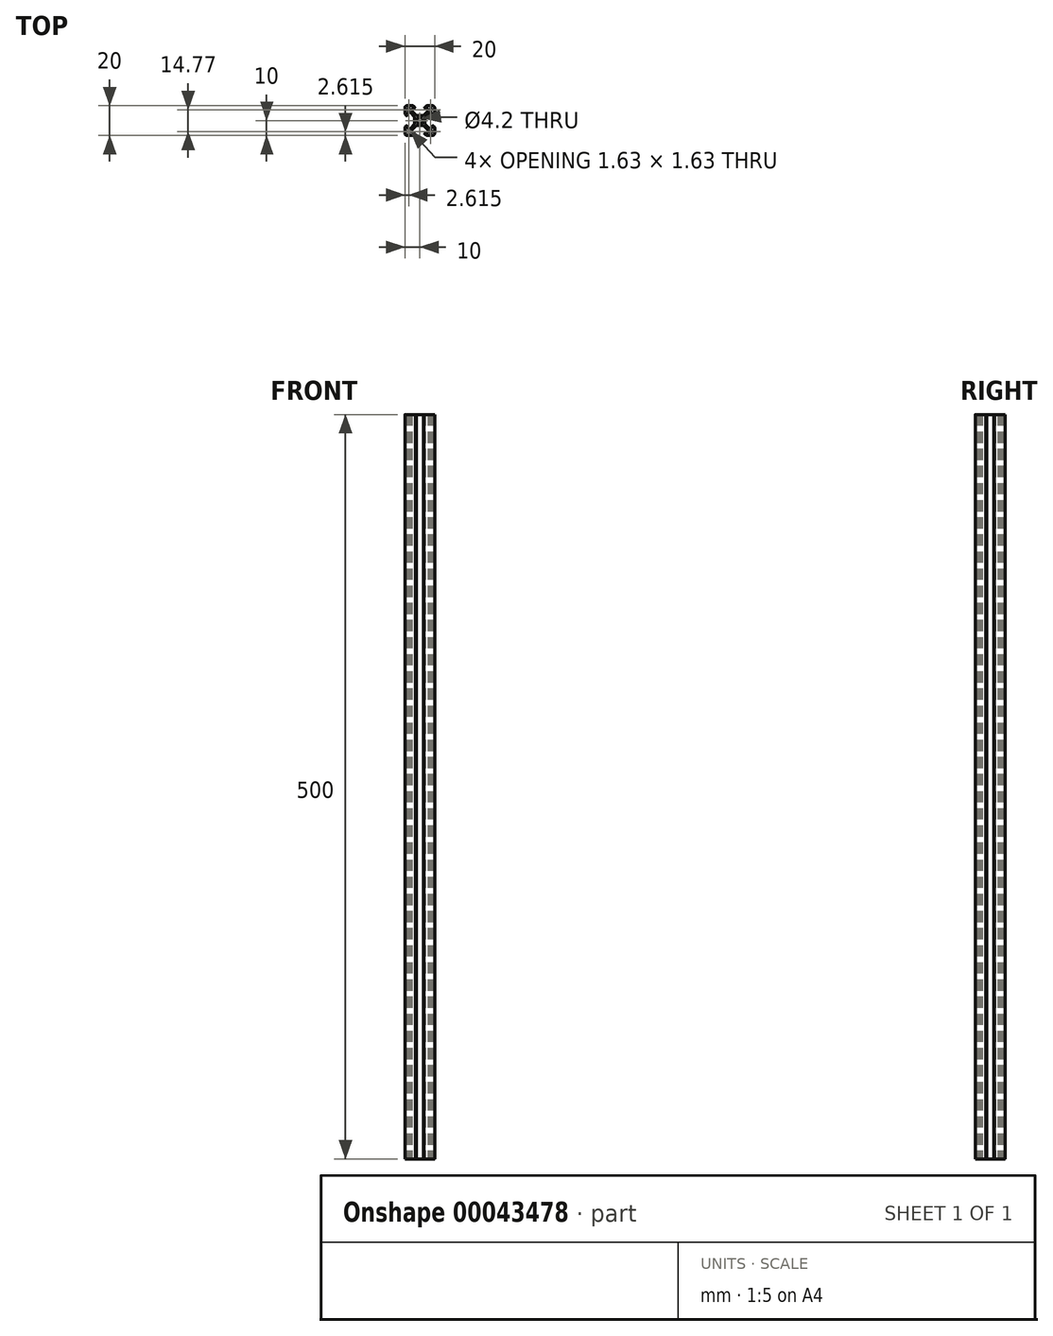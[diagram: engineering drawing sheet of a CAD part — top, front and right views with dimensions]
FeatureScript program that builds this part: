
annotation { "Feature Type Name" : "Feature", "Feature Type Description" : "" }
export const myFeature = defineFeature(function(context is Context, id is Id, definition is map)
    precondition{}
    {
        {
            var Q0;
            Q0=qCreatedBy(makeId("Top.planeOp"),FACE);
            var sketch = newSketch(context, id + "F0", { "sketchPlane" : qUnion([Q0])});
            skLineSegment(sketch, "E0", {"start": v(-8.2, -8.2) * mm, "end": v(-6.57, -8.2) * mm});
            skLineSegment(sketch, "E1", {"start": v(-8.2, -6.57) * mm, "end": v(-8.2, -8.2) * mm});
            skLineSegment(sketch, "E2", {"start": v(-7.66, -6.57) * mm, "end": v(-8.2, -6.57) * mm});
            skLineSegment(sketch, "E3", {"start": v(-6.57, -7.66) * mm, "end": v(-7.66, -6.57) * mm});
            skLineSegment(sketch, "E4", {"start": v(-6.57, -8.2) * mm, "end": v(-6.57, -7.66) * mm});
            skLineSegment(sketch, "E5", {"start": v(7.66, -6.57) * mm, "end": v(6.57, -7.66) * mm});
            skLineSegment(sketch, "E6", {"start": v(8.2, -6.57) * mm, "end": v(7.66, -6.57) * mm});
            skLineSegment(sketch, "E7", {"start": v(8.2, -8.2) * mm, "end": v(8.2, -6.57) * mm});
            skLineSegment(sketch, "E8", {"start": v(6.57, -8.2) * mm, "end": v(8.2, -8.2) * mm});
            skLineSegment(sketch, "E9", {"start": v(6.57, -7.66) * mm, "end": v(6.57, -8.2) * mm});
            skCircle(sketch, "E10", {"center": v(0, 0) * mm, "radius": 2.1 * mm});
            skLineSegment(sketch, "E11", {"start": v(8.2, 8.2) * mm, "end": v(6.57, 8.2) * mm});
            skLineSegment(sketch, "E12", {"start": v(8.2, 6.57) * mm, "end": v(8.2, 8.2) * mm});
            skLineSegment(sketch, "E13", {"start": v(7.66, 6.57) * mm, "end": v(8.2, 6.57) * mm});
            skLineSegment(sketch, "E14", {"start": v(6.57, 7.66) * mm, "end": v(7.66, 6.57) * mm});
            skLineSegment(sketch, "E15", {"start": v(6.57, 8.2) * mm, "end": v(6.57, 7.66) * mm});
            skLineSegment(sketch, "E16", {"start": v(-7.66, 6.57) * mm, "end": v(-6.57, 7.66) * mm});
            skLineSegment(sketch, "E17", {"start": v(-8.2, 6.57) * mm, "end": v(-7.66, 6.57) * mm});
            skLineSegment(sketch, "E18", {"start": v(-8.2, 8.2) * mm, "end": v(-8.2, 6.57) * mm});
            skLineSegment(sketch, "E19", {"start": v(-6.57, 8.2) * mm, "end": v(-8.2, 8.2) * mm});
            skLineSegment(sketch, "E20", {"start": v(-6.57, 7.66) * mm, "end": v(-6.57, 8.2) * mm});
            skLineSegment(sketch, "E21", {"start": v(-6.56, 5.5) * mm, "end": v(-3.4, 2.34) * mm});
            skLineSegment(sketch, "E22", {"start": v(-3.4, 2.34) * mm, "end": v(-3.4, -2.34) * mm});
            skLineSegment(sketch, "E23", {"start": v(-3.4, -2.34) * mm, "end": v(-6.56, -5.5) * mm});
            skLineSegment(sketch, "E24", {"start": v(-6.56, -5.5) * mm, "end": v(-8.2, -5.5) * mm});
            skLineSegment(sketch, "E25", {"start": v(-8.2, -5.5) * mm, "end": v(-8.2, -2.9) * mm});
            skLineSegment(sketch, "E26", {"start": v(-8.2, -2.9) * mm, "end": v(-8.31, -2.9) * mm});
            skLineSegment(sketch, "E27", {"start": v(-8.31, -2.9) * mm, "end": v(-9.77, -4.35) * mm});
            skArc(sketch, "E28", {"start": v(-9.77, -4.35) * mm, "mid": v(-9.94, -4.6) * mm, "end": v(-10, -4.9) * mm});
            skLineSegment(sketch, "E29", {"start": v(-10, -4.9) * mm, "end": v(-10, -8.5) * mm});
            skArc(sketch, "E30", {"start": v(-10, -8.5) * mm, "mid": v(-9.56, -9.56) * mm, "end": v(-8.5, -10) * mm});
            skLineSegment(sketch, "E31", {"start": v(-8.5, -10) * mm, "end": v(-4.9, -10) * mm});
            skArc(sketch, "E32", {"start": v(-4.9, -10) * mm, "mid": v(-4.6, -9.94) * mm, "end": v(-4.35, -9.77) * mm});
            skLineSegment(sketch, "E33", {"start": v(-4.35, -9.77) * mm, "end": v(-2.9, -8.31) * mm});
            skLineSegment(sketch, "E34", {"start": v(-2.9, -8.31) * mm, "end": v(-2.9, -8.2) * mm});
            skLineSegment(sketch, "E35", {"start": v(-2.9, -8.2) * mm, "end": v(-5.5, -8.2) * mm});
            skLineSegment(sketch, "E36", {"start": v(-5.5, -8.2) * mm, "end": v(-5.5, -6.56) * mm});
            skLineSegment(sketch, "E37", {"start": v(-5.5, -6.56) * mm, "end": v(-2.34, -3.4) * mm});
            skLineSegment(sketch, "E38", {"start": v(-2.34, -3.4) * mm, "end": v(2.34, -3.4) * mm});
            skLineSegment(sketch, "E39", {"start": v(2.34, -3.4) * mm, "end": v(5.5, -6.56) * mm});
            skLineSegment(sketch, "E40", {"start": v(5.5, -6.56) * mm, "end": v(5.5, -8.2) * mm});
            skLineSegment(sketch, "E41", {"start": v(5.5, -8.2) * mm, "end": v(2.9, -8.2) * mm});
            skLineSegment(sketch, "E42", {"start": v(2.9, -8.2) * mm, "end": v(2.9, -8.31) * mm});
            skLineSegment(sketch, "E43", {"start": v(2.9, -8.31) * mm, "end": v(4.35, -9.77) * mm});
            skArc(sketch, "E44", {"start": v(4.35, -9.77) * mm, "mid": v(4.6, -9.94) * mm, "end": v(4.9, -10) * mm});
            skLineSegment(sketch, "E45", {"start": v(4.9, -10) * mm, "end": v(8.5, -10) * mm});
            skArc(sketch, "E46", {"start": v(8.5, -10) * mm, "mid": v(9.56, -9.56) * mm, "end": v(10, -8.5) * mm});
            skLineSegment(sketch, "E47", {"start": v(10, -8.5) * mm, "end": v(10, -4.9) * mm});
            skArc(sketch, "E48", {"start": v(10, -4.9) * mm, "mid": v(9.94, -4.6) * mm, "end": v(9.77, -4.35) * mm});
            skLineSegment(sketch, "E49", {"start": v(9.77, -4.35) * mm, "end": v(8.31, -2.9) * mm});
            skLineSegment(sketch, "E50", {"start": v(8.31, -2.9) * mm, "end": v(8.2, -2.9) * mm});
            skLineSegment(sketch, "E51", {"start": v(8.2, -2.9) * mm, "end": v(8.2, -5.5) * mm});
            skLineSegment(sketch, "E52", {"start": v(8.2, -5.5) * mm, "end": v(6.56, -5.5) * mm});
            skLineSegment(sketch, "E53", {"start": v(6.56, -5.5) * mm, "end": v(3.4, -2.34) * mm});
            skLineSegment(sketch, "E54", {"start": v(3.4, -2.34) * mm, "end": v(3.4, 2.34) * mm});
            skLineSegment(sketch, "E55", {"start": v(3.4, 2.34) * mm, "end": v(6.56, 5.5) * mm});
            skLineSegment(sketch, "E56", {"start": v(6.56, 5.5) * mm, "end": v(8.2, 5.5) * mm});
            skLineSegment(sketch, "E57", {"start": v(8.2, 5.5) * mm, "end": v(8.2, 2.9) * mm});
            skLineSegment(sketch, "E58", {"start": v(8.2, 2.9) * mm, "end": v(8.31, 2.9) * mm});
            skLineSegment(sketch, "E59", {"start": v(8.31, 2.9) * mm, "end": v(9.77, 4.35) * mm});
            skArc(sketch, "E60", {"start": v(9.77, 4.35) * mm, "mid": v(9.94, 4.6) * mm, "end": v(10, 4.9) * mm});
            skLineSegment(sketch, "E61", {"start": v(10, 4.9) * mm, "end": v(10, 8.5) * mm});
            skArc(sketch, "E62", {"start": v(10, 8.5) * mm, "mid": v(9.56, 9.56) * mm, "end": v(8.5, 10) * mm});
            skLineSegment(sketch, "E63", {"start": v(8.5, 10) * mm, "end": v(4.9, 10) * mm});
            skArc(sketch, "E64", {"start": v(4.9, 10) * mm, "mid": v(4.6, 9.94) * mm, "end": v(4.35, 9.77) * mm});
            skLineSegment(sketch, "E65", {"start": v(4.35, 9.77) * mm, "end": v(2.9, 8.31) * mm});
            skLineSegment(sketch, "E66", {"start": v(2.9, 8.31) * mm, "end": v(2.9, 8.2) * mm});
            skLineSegment(sketch, "E67", {"start": v(2.9, 8.2) * mm, "end": v(5.5, 8.2) * mm});
            skLineSegment(sketch, "E68", {"start": v(5.5, 8.2) * mm, "end": v(5.5, 6.56) * mm});
            skLineSegment(sketch, "E69", {"start": v(5.5, 6.56) * mm, "end": v(2.34, 3.4) * mm});
            skLineSegment(sketch, "E70", {"start": v(2.34, 3.4) * mm, "end": v(-2.34, 3.4) * mm});
            skLineSegment(sketch, "E71", {"start": v(-2.34, 3.4) * mm, "end": v(-5.5, 6.56) * mm});
            skLineSegment(sketch, "E72", {"start": v(-5.5, 6.56) * mm, "end": v(-5.5, 8.2) * mm});
            skLineSegment(sketch, "E73", {"start": v(-5.5, 8.2) * mm, "end": v(-2.9, 8.2) * mm});
            skLineSegment(sketch, "E74", {"start": v(-2.9, 8.2) * mm, "end": v(-2.9, 8.31) * mm});
            skLineSegment(sketch, "E75", {"start": v(-2.9, 8.31) * mm, "end": v(-4.35, 9.77) * mm});
            skArc(sketch, "E76", {"start": v(-4.35, 9.77) * mm, "mid": v(-4.6, 9.94) * mm, "end": v(-4.9, 10) * mm});
            skLineSegment(sketch, "E77", {"start": v(-4.9, 10) * mm, "end": v(-8.5, 10) * mm});
            skArc(sketch, "E78", {"start": v(-8.5, 10) * mm, "mid": v(-9.56, 9.56) * mm, "end": v(-10, 8.5) * mm});
            skLineSegment(sketch, "E79", {"start": v(-10, 8.5) * mm, "end": v(-10, 4.9) * mm});
            skArc(sketch, "E80", {"start": v(-10, 4.9) * mm, "mid": v(-9.94, 4.6) * mm, "end": v(-9.77, 4.35) * mm});
            skLineSegment(sketch, "E81", {"start": v(-9.77, 4.35) * mm, "end": v(-8.31, 2.9) * mm});
            skLineSegment(sketch, "E82", {"start": v(-8.31, 2.9) * mm, "end": v(-8.2, 2.9) * mm});
            skLineSegment(sketch, "E83", {"start": v(-8.2, 2.9) * mm, "end": v(-8.2, 5.5) * mm});
            skLineSegment(sketch, "E84", {"start": v(-8.2, 5.5) * mm, "end": v(-6.56, 5.5) * mm});
            skSolve(sketch);
        }
        {
            var Q0;
            Q0=qSketchRegion(id+"F0",true);
            extrude(context, id + "F1", {"entities" : qUnion([Q0]), "depth" : 500 * mm});
        }
    });
